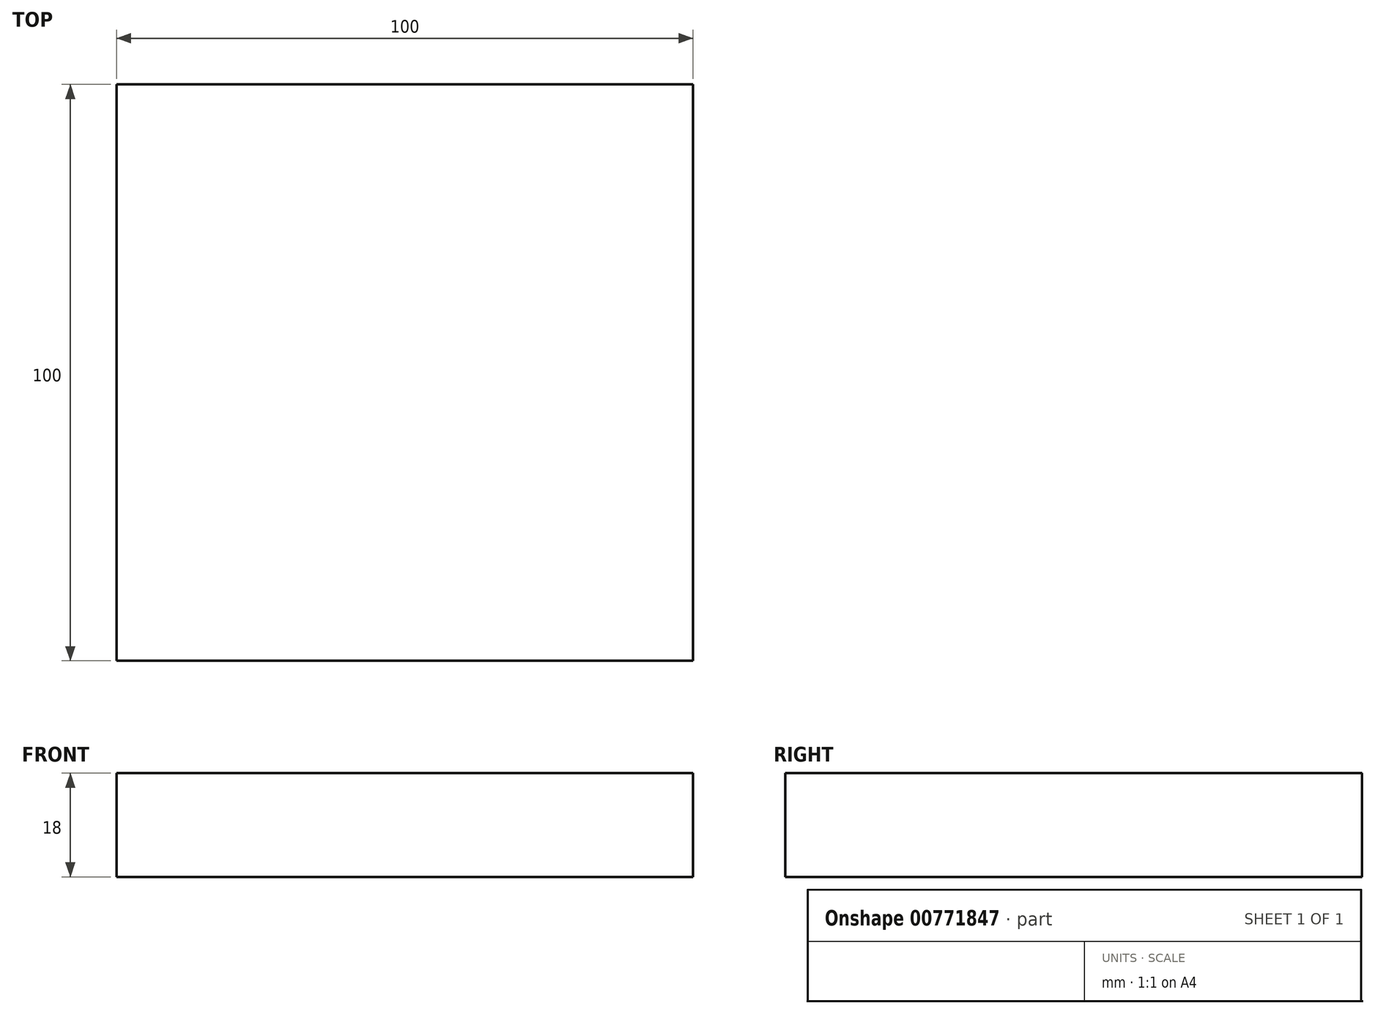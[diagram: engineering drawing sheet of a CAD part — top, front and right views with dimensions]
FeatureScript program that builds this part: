
annotation { "Feature Type Name" : "Feature", "Feature Type Description" : "" }
export const myFeature = defineFeature(function(context is Context, id is Id, definition is map)
    precondition{}
    {
        {
            var Q0;
            Q0=qCreatedBy(makeId("Front.planeOp"),FACE);
            var sketch = newSketch(context, id + "F0", { "sketchPlane" : qUnion([Q0])});
            skLineSegment(sketch, "E0.bottom", {"start": v(0, 0) * mm, "end": v(-100, 0) * mm});
            skLineSegment(sketch, "E0.top", {"start": v(0, 18) * mm, "end": v(-100, 18) * mm});
            skLineSegment(sketch, "E0.left", {"start": v(0, 0) * mm, "end": v(0, 18) * mm});
            skLineSegment(sketch, "E0.right", {"start": v(-100, 0) * mm, "end": v(-100, 18) * mm});
            skSolve(sketch);
        }
        {
            var Q0;
            Q0=makeQuery(id+"F0.imprint","IMPRINT",FACE,{"disambiguationData":[TD([[makeQuery(id+"F0.imprint","IMPRINT",EDGE,{"derivedFrom":sQuery(id+"F0.wireOp",EDGE,"E0.bottom")}),-1.0]])]});
            extrude(context, id + "F1", {"entities" : qUnion([Q0]), "endBound" : BoundingType.SYMMETRIC, "depth" : 100 * mm, "offsetDistance" : 25 * mm});
        }
    });
